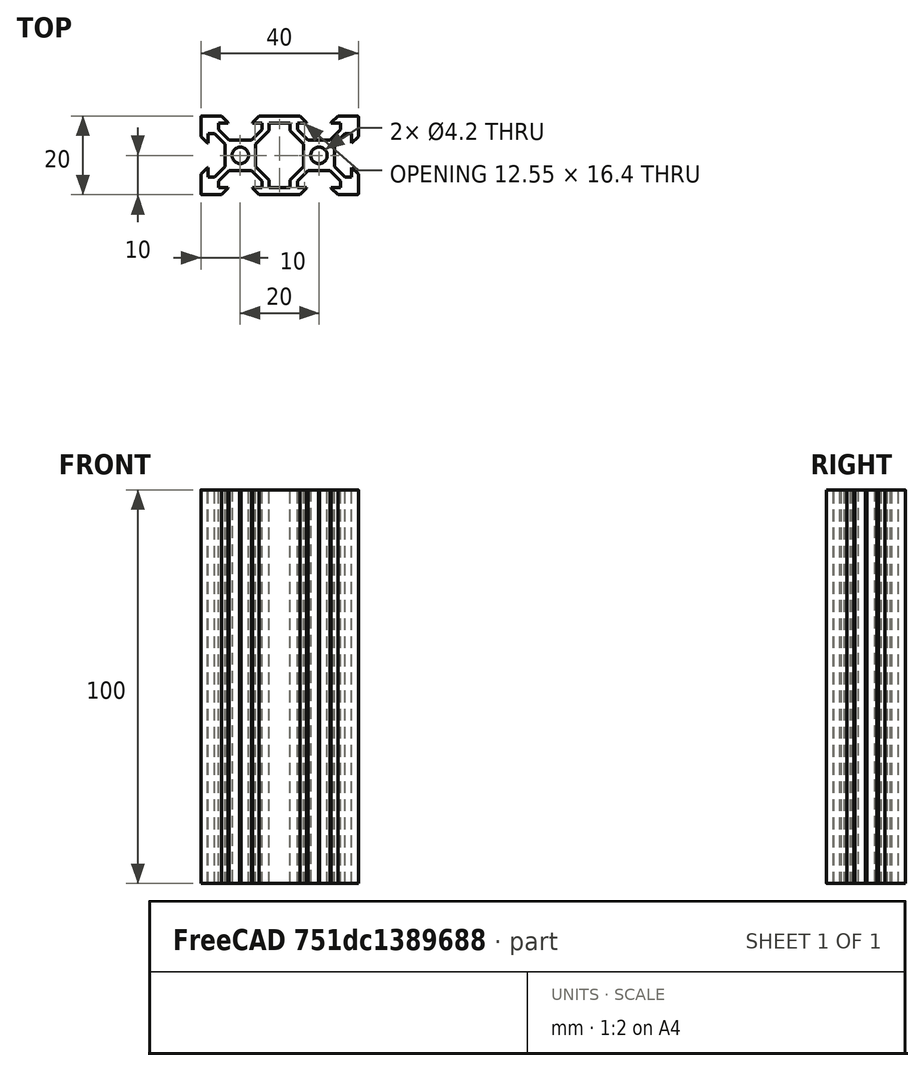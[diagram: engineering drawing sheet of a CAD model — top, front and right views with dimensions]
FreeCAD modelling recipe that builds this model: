
FCSTD DOCUMENT  (FreeCAD 0.19R23578 (Git))
Label: VSLOT_4020
License: All rights reserved
LicenseURL: http://en.wikipedia.org/wiki/All_rights_reserved
objects: Sketcher::SketchObject×1, PartDesign::Pad×1, PartDesign::Chamfer×1, PartDesign::Fillet×1, PartDesign::Body×1, App::Part×1
note: 8 computed .brp shape members not serialized (recipe doc carries the construction recipe); baked Part::Feature solids carry a one-line shape summary decoded from their .brp

FEATURE [Sketcher::SketchObject] Sketch
  MapMode = 5
  Support = -> [XY_Plane001]
  sketch-geometry (102):
    g0: LineSegment StartX=0 StartY=3.72388 StartZ=0 EndX=0.176777 EndY=3.90066 EndZ=0
    g1: LineSegment StartX=0.176777 StartY=3.90066 StartZ=0 EndX=2.84 EndY=3.90066 EndZ=0
    g2: LineSegment StartX=2.84 StartY=3.90066 StartZ=0 EndX=5.49934 EndY=6.56 EndZ=0
    g3: LineSegment StartX=5.49934 StartY=6.56 StartZ=0 EndX=5.49934 EndY=8.2 EndZ=0
    g4: LineSegment StartX=5.49934 StartY=8.2 StartZ=0 EndX=3.1 EndY=8.2 EndZ=0
    g5: LineSegment StartX=3.1 StartY=8.2 StartZ=0 EndX=3.1 EndY=10 EndZ=0
    g6: LineSegment StartX=3.1 StartY=10 StartZ=0 EndX=16.9 EndY=10 EndZ=0
    g7: LineSegment StartX=7.29934 StartY=6.23868 StartZ=0 EndX=3.90066 EndY=2.84 EndZ=0
    g8: LineSegment StartX=3.90066 StartY=2.84 StartZ=0 EndX=3.90066 EndY=0.176777 EndZ=0
    g9: LineSegment StartX=3.90066 StartY=0.176777 StartZ=0 EndX=3.72388 EndY=0 EndZ=0
    g10: LineSegment StartX=0 StartY=3.72388 StartZ=0 EndX=-0.176777 EndY=3.90066 EndZ=0
    g11: LineSegment StartX=-0.176777 StartY=3.90066 StartZ=0 EndX=-2.84 EndY=3.90066 EndZ=0
    g12: LineSegment StartX=-2.84 StartY=3.90066 StartZ=0 EndX=-5.49934 EndY=6.56 EndZ=0
    g13: LineSegment StartX=-5.49934 StartY=6.56 StartZ=0 EndX=-5.49934 EndY=8.2 EndZ=0
    g14: LineSegment StartX=-5.49934 StartY=8.2 StartZ=0 EndX=-3.1 EndY=8.2 EndZ=0
    g15: LineSegment StartX=-3.1 StartY=8.2 StartZ=0 EndX=-3.1 EndY=10 EndZ=0
    g16: LineSegment StartX=-3.1 StartY=10 StartZ=0 EndX=-10 EndY=10 EndZ=0
    g17: LineSegment StartX=-10 StartY=10 StartZ=0 EndX=-10 EndY=3.1 EndZ=0
    g18: LineSegment StartX=-10 StartY=3.1 StartZ=0 EndX=-8.2 EndY=3.1 EndZ=0
    g19: LineSegment StartX=-8.2 StartY=3.1 StartZ=0 EndX=-8.2 EndY=5.49934 EndZ=0
    g20: LineSegment StartX=-8.2 StartY=5.49934 StartZ=0 EndX=-6.56 EndY=5.49934 EndZ=0
    g21: LineSegment StartX=-6.56 StartY=5.49934 StartZ=0 EndX=-3.90066 EndY=2.84 EndZ=0
    g22: LineSegment StartX=-3.90066 StartY=2.84 StartZ=0 EndX=-3.90066 EndY=0.176777 EndZ=0
    g23: LineSegment StartX=-3.90066 StartY=0.176777 StartZ=0 EndX=-3.72388 EndY=0 EndZ=0
    g24: LineSegment StartX=0 StartY=-3.72388 StartZ=0 EndX=0.176777 EndY=-3.90066 EndZ=0
    g25: LineSegment StartX=0.176777 StartY=-3.90066 StartZ=0 EndX=2.84 EndY=-3.90066 EndZ=0
    g26: LineSegment StartX=2.84 StartY=-3.90066 StartZ=0 EndX=5.49934 EndY=-6.56 EndZ=0
    g27: LineSegment StartX=5.49934 StartY=-6.56 StartZ=0 EndX=5.49934 EndY=-8.2 EndZ=0
    g28: LineSegment StartX=5.49934 StartY=-8.2 StartZ=0 EndX=3.1 EndY=-8.2 EndZ=0
    g29: LineSegment StartX=3.1 StartY=-8.2 StartZ=0 EndX=3.1 EndY=-10 EndZ=0
    g30: LineSegment StartX=3.1 StartY=-10 StartZ=0 EndX=16.9 EndY=-10 EndZ=0
    g31: LineSegment StartX=7.29934 StartY=-6.23868 StartZ=0 EndX=3.90066 EndY=-2.84 EndZ=0
    g32: LineSegment StartX=3.90066 StartY=-2.84 StartZ=0 EndX=3.90066 EndY=-0.176777 EndZ=0
    g33: LineSegment StartX=3.90066 StartY=-0.176777 StartZ=0 EndX=3.72388 EndY=0 EndZ=0
    g34: LineSegment StartX=0 StartY=-3.72388 StartZ=0 EndX=-0.176777 EndY=-3.90066 EndZ=0
    g35: LineSegment StartX=-0.176777 StartY=-3.90066 StartZ=0 EndX=-2.84 EndY=-3.90066 EndZ=0
    g36: LineSegment StartX=-2.84 StartY=-3.90066 StartZ=0 EndX=-5.49934 EndY=-6.56 EndZ=0
    g37: LineSegment StartX=-5.49934 StartY=-6.56 StartZ=0 EndX=-5.49934 EndY=-8.2 EndZ=0
    g38: LineSegment StartX=-5.49934 StartY=-8.2 StartZ=0 EndX=-3.1 EndY=-8.2 EndZ=0
    g39: LineSegment StartX=-3.1 StartY=-8.2 StartZ=0 EndX=-3.1 EndY=-10 EndZ=0
    g40: LineSegment StartX=-3.1 StartY=-10 StartZ=0 EndX=-10 EndY=-10 EndZ=0
    g41: LineSegment StartX=-10 StartY=-10 StartZ=0 EndX=-10 EndY=-3.1 EndZ=0
    g42: LineSegment StartX=-10 StartY=-3.1 StartZ=0 EndX=-8.2 EndY=-3.1 EndZ=0
    g43: LineSegment StartX=-8.2 StartY=-3.1 StartZ=0 EndX=-8.2 EndY=-5.49934 EndZ=0
    g44: LineSegment StartX=-8.2 StartY=-5.49934 StartZ=0 EndX=-6.56 EndY=-5.49934 EndZ=0
    g45: LineSegment StartX=-6.56 StartY=-5.49934 StartZ=0 EndX=-3.90066 EndY=-2.84 EndZ=0
    g46: LineSegment StartX=-3.90066 StartY=-2.84 StartZ=0 EndX=-3.90066 EndY=-0.176777 EndZ=0
    g47: LineSegment StartX=-3.90066 StartY=-0.176777 StartZ=0 EndX=-3.72388 EndY=0 EndZ=0
    g48: Circle CenterX=0 CenterY=0 CenterZ=0 NormalX=0 NormalY=0 NormalZ=1 AngleXU=0 Radius=2.1
    g49: LineSegment StartX=20 StartY=3.72388 StartZ=0 EndX=19.8232 EndY=3.90066 EndZ=0
    g50: LineSegment StartX=19.8232 StartY=3.90066 StartZ=0 EndX=17.16 EndY=3.90066 EndZ=0
    g51: LineSegment StartX=17.16 StartY=3.90066 StartZ=0 EndX=14.5007 EndY=6.56 EndZ=0
    g52: LineSegment StartX=14.5007 StartY=6.56 StartZ=0 EndX=14.5007 EndY=8.2 EndZ=0
    g53: LineSegment StartX=14.5007 StartY=8.2 StartZ=0 EndX=16.9 EndY=8.2 EndZ=0
    g54: LineSegment StartX=16.9 StartY=8.2 StartZ=0 EndX=16.9 EndY=10 EndZ=0
    g55: LineSegment StartX=12.7007 StartY=6.23868 StartZ=0 EndX=16.0993 EndY=2.84 EndZ=0
    g56: LineSegment StartX=16.0993 StartY=2.84 StartZ=0 EndX=16.0993 EndY=0.176777 EndZ=0
    g57: LineSegment StartX=16.0993 StartY=0.176777 StartZ=0 EndX=16.2761 EndY=3.6e-15 EndZ=0
    g58: LineSegment StartX=20 StartY=3.72388 StartZ=0 EndX=20.1768 EndY=3.90066 EndZ=0
    g59: LineSegment StartX=20.1768 StartY=3.90066 StartZ=0 EndX=22.84 EndY=3.90066 EndZ=0
    g60: LineSegment StartX=22.84 StartY=3.90066 StartZ=0 EndX=25.4993 EndY=6.56 EndZ=0
    g61: LineSegment StartX=25.4993 StartY=6.56 StartZ=0 EndX=25.4993 EndY=8.2 EndZ=0
    g62: LineSegment StartX=25.4993 StartY=8.2 StartZ=0 EndX=23.1 EndY=8.2 EndZ=0
    g63: LineSegment StartX=23.1 StartY=8.2 StartZ=0 EndX=23.1 EndY=10 EndZ=0
    g64: LineSegment StartX=23.1 StartY=10 StartZ=0 EndX=30 EndY=10 EndZ=0
    g65: LineSegment StartX=30 StartY=10 StartZ=0 EndX=30 EndY=3.1 EndZ=0
    g66: LineSegment StartX=30 StartY=3.1 StartZ=0 EndX=28.2 EndY=3.1 EndZ=0
    g67: LineSegment StartX=28.2 StartY=3.1 StartZ=0 EndX=28.2 EndY=5.49934 EndZ=0
    g68: LineSegment StartX=28.2 StartY=5.49934 StartZ=0 EndX=26.56 EndY=5.49934 EndZ=0
    g69: LineSegment StartX=26.56 StartY=5.49934 StartZ=0 EndX=23.9007 EndY=2.84 EndZ=0
    g70: LineSegment StartX=23.9007 StartY=2.84 StartZ=0 EndX=23.9007 EndY=0.176777 EndZ=0
    g71: LineSegment StartX=23.9007 StartY=0.176777 StartZ=0 EndX=23.7239 EndY=3.6e-15 EndZ=0
    g72: LineSegment StartX=20 StartY=-3.72388 StartZ=0 EndX=19.8232 EndY=-3.90066 EndZ=0
    g73: LineSegment StartX=19.8232 StartY=-3.90066 StartZ=0 EndX=17.16 EndY=-3.90066 EndZ=0
    g74: LineSegment StartX=17.16 StartY=-3.90066 StartZ=0 EndX=14.5007 EndY=-6.56 EndZ=0
    g75: LineSegment StartX=14.5007 StartY=-6.56 StartZ=0 EndX=14.5007 EndY=-8.2 EndZ=0
    g76: LineSegment StartX=14.5007 StartY=-8.2 StartZ=0 EndX=16.9 EndY=-8.2 EndZ=0
    g77: LineSegment StartX=16.9 StartY=-8.2 StartZ=0 EndX=16.9 EndY=-10 EndZ=0
    g78: LineSegment StartX=12.7007 StartY=-6.23868 StartZ=0 EndX=16.0993 EndY=-2.84 EndZ=0
    g79: LineSegment StartX=16.0993 StartY=-2.84 StartZ=0 EndX=16.0993 EndY=-0.176777 EndZ=0
    g80: LineSegment StartX=16.0993 StartY=-0.176777 StartZ=0 EndX=16.2761 EndY=3.6e-15 EndZ=0
    g81: LineSegment StartX=20 StartY=-3.72388 StartZ=0 EndX=20.1768 EndY=-3.90066 EndZ=0
    g82: LineSegment StartX=20.1768 StartY=-3.90066 StartZ=0 EndX=22.84 EndY=-3.90066 EndZ=0
    g83: LineSegment StartX=22.84 StartY=-3.90066 StartZ=0 EndX=25.4993 EndY=-6.56 EndZ=0
    g84: LineSegment StartX=25.4993 StartY=-6.56 StartZ=0 EndX=25.4993 EndY=-8.2 EndZ=0
    g85: LineSegment StartX=25.4993 StartY=-8.2 StartZ=0 EndX=23.1 EndY=-8.2 EndZ=0
    g86: LineSegment StartX=23.1 StartY=-8.2 StartZ=0 EndX=23.1 EndY=-10 EndZ=0
    g87: LineSegment StartX=23.1 StartY=-10 StartZ=0 EndX=30 EndY=-10 EndZ=0
    g88: LineSegment StartX=30 StartY=-10 StartZ=0 EndX=30 EndY=-3.1 EndZ=0
    g89: LineSegment StartX=30 StartY=-3.1 StartZ=0 EndX=28.2 EndY=-3.1 EndZ=0
    g90: LineSegment StartX=28.2 StartY=-3.1 StartZ=0 EndX=28.2 EndY=-5.49934 EndZ=0
    g91: LineSegment StartX=28.2 StartY=-5.49934 StartZ=0 EndX=26.56 EndY=-5.49934 EndZ=0
    g92: LineSegment StartX=26.56 StartY=-5.49934 StartZ=0 EndX=23.9007 EndY=-2.84 EndZ=0
    g93: LineSegment StartX=23.9007 StartY=-2.84 StartZ=0 EndX=23.9007 EndY=-0.176777 EndZ=0
    g94: LineSegment StartX=23.9007 StartY=-0.176777 StartZ=0 EndX=23.7239 EndY=3.6e-15 EndZ=0
    g95: Circle CenterX=20 CenterY=3.6e-15 CenterZ=0 NormalX=0 NormalY=0 NormalZ=1 AngleXU=0 Radius=2.1
    g96: LineSegment StartX=7.29934 StartY=-6.23868 StartZ=0 EndX=7.29934 EndY=-8.2 EndZ=0
    g97: LineSegment StartX=7.29934 StartY=-8.2 StartZ=0 EndX=12.7007 EndY=-8.2 EndZ=0
    g98: LineSegment StartX=12.7007 StartY=-8.2 StartZ=0 EndX=12.7007 EndY=-6.23868 EndZ=0
    g99: LineSegment StartX=7.29934 StartY=6.23868 StartZ=0 EndX=7.29934 EndY=8.2 EndZ=0
    g100: LineSegment StartX=7.29934 StartY=8.2 StartZ=0 EndX=12.7007 EndY=8.2 EndZ=0
    g101: LineSegment StartX=12.7007 StartY=8.2 StartZ=0 EndX=12.7007 EndY=6.23868 EndZ=0
  constraints (20):
    c: Block(g74)
    c: Block(g75)
    c: Block(g79)
    c: Block(g32)
    c: Block(g26)
    c: Block(g27)
    c: Coincident(g97,g96)
    c: Vertical(g96)
    c: Vertical(g98)
    c: Coincident(g98,g97)
    c: Horizontal(g97)
    c: Horizontal(g100)
    c: Parallel(g26,g31)
    c: Parallel(g74,g78)
    c: DistanceX(g27,g96) = 1.8
    c: Coincident(g31,g96)
    c: Coincident(g32,g31)
    c: DistanceX(g97,g75) = 1.8
    c: Coincident(g78,g98)
    c: Coincident(g79,g78)
FEATURE [PartDesign::Pad] Pad
  Direction = (1,1,1)
  Length = 100
  Length2 = 100
  Profile = -> Sketch
  Type = 0
FEATURE [PartDesign::Chamfer] Chamfer
  Angle = 45
  Base = -> Pad [Edge146,Edge143,Edge107,Edge182,Edge101,Edge65,Edge59,Edge23,Edge20,Edge230,Edge188,Edge224]
  BaseFeature = -> Pad
  ChamferType = 2
  FlipDirection = false
  Size = 1.7
  Size2 = 1
  SupportTransform = false
FEATURE [PartDesign::Fillet] Fillet
  Base = -> Chamfer [Edge288,Edge256,Edge263,Edge295]
  BaseFeature = -> Chamfer
  Radius = 0.2
  SupportTransform = false
FEATURE [PartDesign::Body] Body
  Group = -> [Sketch,Pad,Chamfer,Fillet]
  Origin = -> Origin001
  Tip = -> Fillet
FEATURE [App::Part] Part
  Group = -> [Body]
  Origin = -> Origin
